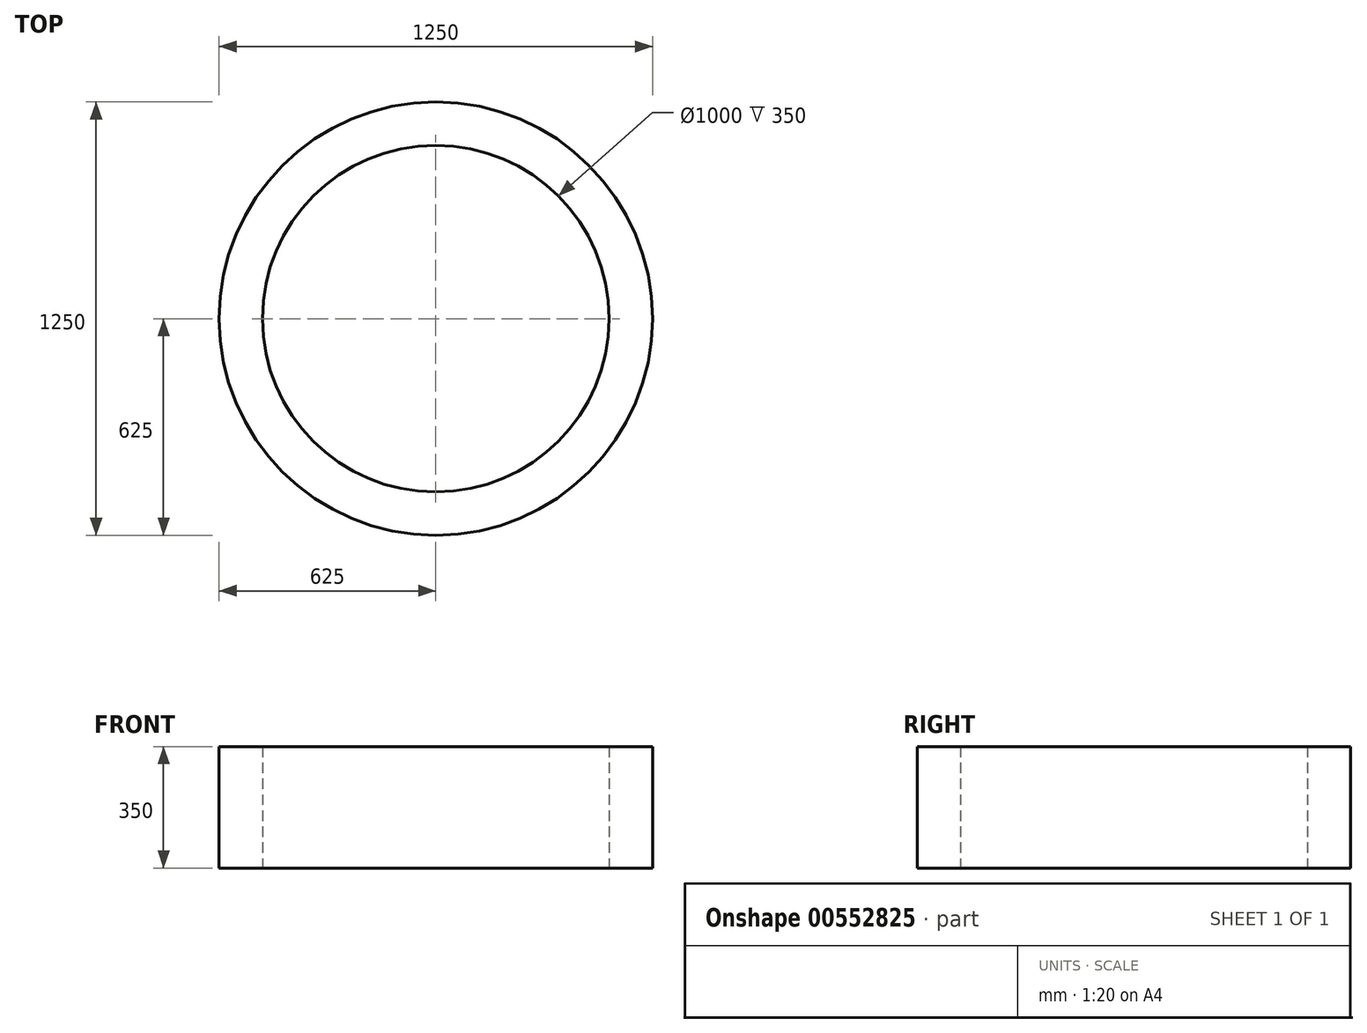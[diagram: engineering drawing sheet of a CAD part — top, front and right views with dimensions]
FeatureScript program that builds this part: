
annotation { "Feature Type Name" : "Feature", "Feature Type Description" : "" }
export const myFeature = defineFeature(function(context is Context, id is Id, definition is map)
    precondition{}
    {
        {
            var Q0;
            Q0=qCreatedBy(makeId("Top.planeOp"),FACE);
            var sketch = newSketch(context, id + "F0", { "sketchPlane" : qUnion([Q0])});
            skCircle(sketch, "E0", {"center": v(0, 0) * mm, "radius": 500 * mm});
            skCircle(sketch, "E1", {"center": v(0, 0) * mm, "radius": 625 * mm});
            skSolve(sketch);
        }
        {
            var Q0;
            Q0 = qSketchRegion(id + "F0", true);
            extrude(context, id + "F1", {"entities" : qUnion([Q0]), "depth" : 350 * mm, "offsetDistance" : 25 * mm});
        }
    });
